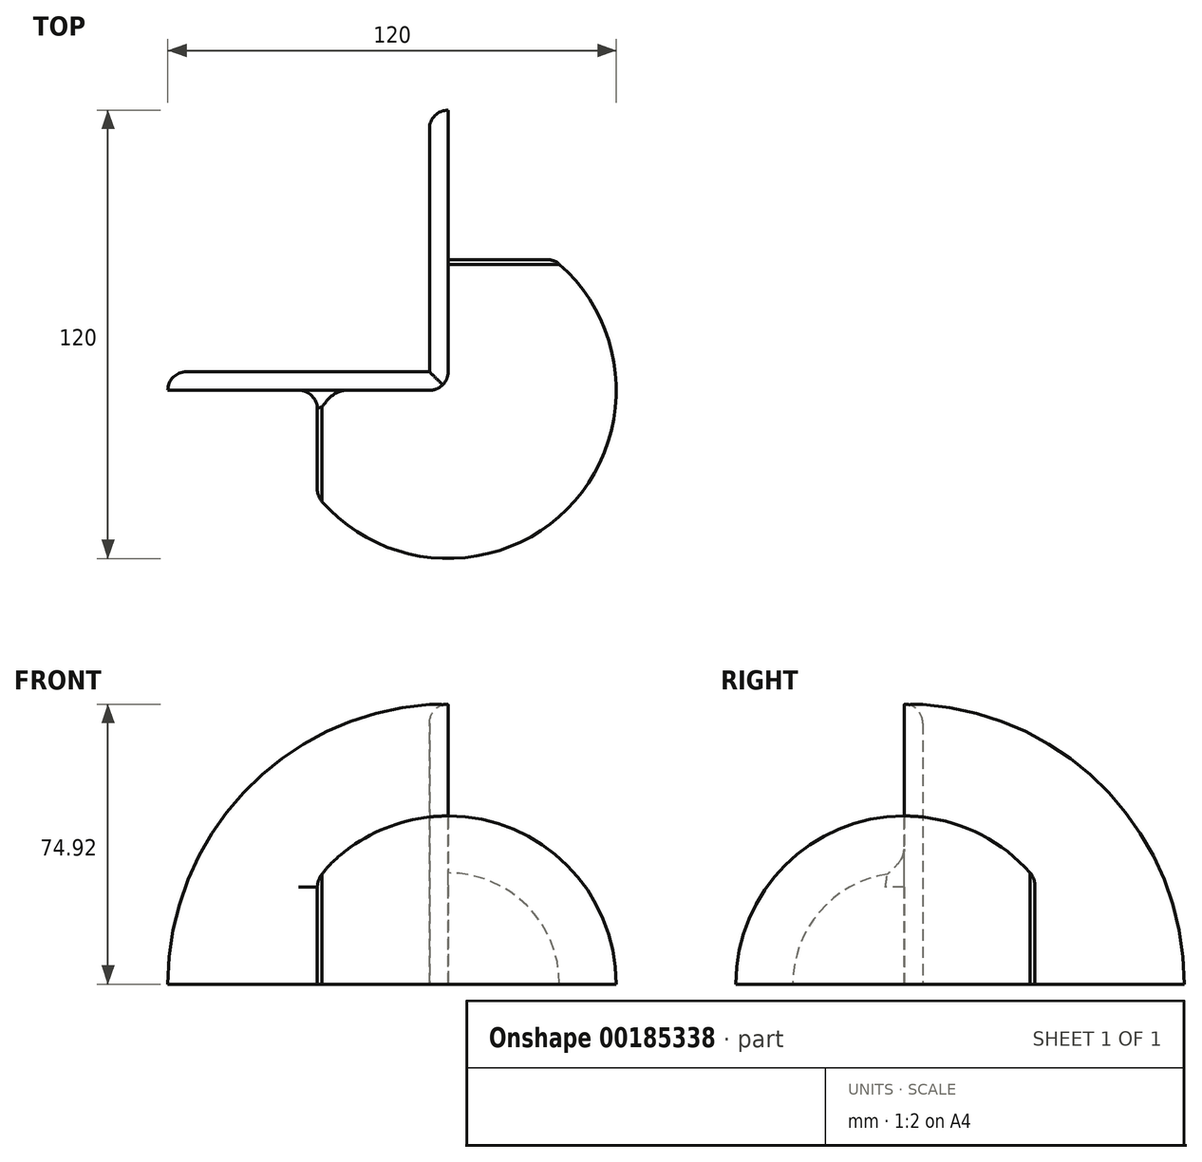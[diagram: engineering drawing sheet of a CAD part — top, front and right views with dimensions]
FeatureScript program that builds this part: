
annotation { "Feature Type Name" : "Feature", "Feature Type Description" : "" }
export const myFeature = defineFeature(function(context is Context, id is Id, definition is map)
    precondition{}
    {
        {
            var Q0;
            Q0=qCreatedBy(makeId("Front.planeOp"),FACE);
            var sketch = newSketch(context, id + "F0", { "sketchPlane" : qUnion([Q0])});
            skArc(sketch, "E0", {"start": v(0, 45) * mm, "mid": v(-31.82, 31.82) * mm, "end": v(-45, 0) * mm});
            skLineSegment(sketch, "E1", {"start": v(-45, 0) * mm, "end": v(0, 0) * mm});
            skLineSegment(sketch, "E2", {"start": v(0, 0) * mm, "end": v(0, 45) * mm});
            skSolve(sketch);
        }
        {
            var Q0;
            Q0 = qSketchRegion(id + "F0", true);
            var Q1;
            Q1=sQuery(id+"F0.wireOp",EDGE,"E2");
            revolve(context, id + "F1", {"entities" : qUnion([Q0]), "axis" : qUnion([Q1]), "revolveType" : RevolveType.ONE_DIRECTION, "angle" : 270 * degree});
        }
        {
            var Q0;
            Q0=makeQuery(id+"F1.opRevolve","CAP_FACE",FACE,{"disambiguationData":[OSD([sQuery(id+"F0.wireOp",EDGE,"E0"),sQuery(id+"F0.wireOp",EDGE,"E1"),sQuery(id+"F0.wireOp",EDGE,"E2")])],"isStart":true});
            var sketch = newSketch(context, id + "F2", { "sketchPlane" : qUnion([Q0])});
            skLineSegment(sketch, "E3", {"start": v(0, 0) * mm, "end": v(0, 75) * mm});
            skLineSegment(sketch, "E4", {"start": v(0, 0) * mm, "end": v(75, 0) * mm});
            skArc(sketch, "E5", {"start": v(75, 0) * mm, "mid": v(53.03, 53.03) * mm, "end": v(0, 75) * mm});
            skSolve(sketch);
        }
        {
            var Q0;
            Q0 = qSketchRegion(id + "F2", true);
            var Q1;
            Q1=sQuery(id+"F2.wireOp",EDGE,"E3");
            revolve(context, id + "F3", {"operationType" : NewBodyOperationType.ADD, "entities" : qUnion([Q0]), "axis" : qUnion([Q1]), "revolveType" : RevolveType.ONE_DIRECTION, "oppositeDirection" : true, "angle" : 90 * degree});
        }
        {
            var Q0;
            Q0=makeQuery(id+"F3.boolean.opBoolean","MERGE",FACE,{"derivedFrom":[makeQuery(id+"F1.opRevolve","SWEPT_FACE",FACE,{"disambiguationData":[OSD([sQuery(id+"F0.wireOp",EDGE,"E1")])]}),makeQuery(id+"F3.opRevolve","SWEPT_FACE",FACE,{"disambiguationData":[OSD([sQuery(id+"F2.wireOp",EDGE,"E4")])]})]});
            var sketch = newSketch(context, id + "F4", { "sketchPlane" : qUnion([Q0])});
            skLineSegment(sketch, "E6", {"start": v(-5, -74.83) * mm, "end": v(-5, -5) * mm});
            skLineSegment(sketch, "E7", {"start": v(-5, -5) * mm, "end": v(-74.83, -5) * mm});
            skArc(sketch, "E8.0", {"start": v(0, -75) * mm, "mid": v(-53.03, -53.03) * mm, "end": v(-75, 0) * mm});
            skLineSegment(sketch, "E9", {"start": v(-45, 0) * mm, "end": v(-35, 0) * mm});
            skLineSegment(sketch, "E10", {"start": v(-35, 0) * mm, "end": v(-35, 28.28) * mm});
            skArc(sketch, "E11.0", {"start": v(0, -45) * mm, "mid": v(31.82, 31.82) * mm, "end": v(-45, 0) * mm});
            skLineSegment(sketch, "E12", {"start": v(0, -35) * mm, "end": v(28.28, -35) * mm});
            skLineSegment(sketch, "E13", {"start": v(0, -35) * mm, "end": v(0, -45) * mm});
            skLineSegment(sketch, "E14", {"start": v(-5, -74.83) * mm, "end": v(10.24, -87.79) * mm});
            skLineSegment(sketch, "E15", {"start": v(10.24, -87.79) * mm, "end": v(15.24, -87.79) * mm});
            skLineSegment(sketch, "E16", {"start": v(15.24, -87.79) * mm, "end": v(0, -75) * mm});
            skPoint(sketch, "E17", {"position": v(-53.03, -53.03) * mm});
            skLineSegment(sketch, "E18", {"start": v(0, 0) * mm, "end": v(-53.03, -53.03) * mm, "construction": true});
            skLineSegment(sketch, "E19", {"start": v(-74.83, -5) * mm, "end": v(-88.25, 9.83) * mm});
            skLineSegment(sketch, "E20", {"start": v(-83.25, 9.83) * mm, "end": v(-75, 0) * mm});
            skLineSegment(sketch, "E21", {"start": v(-88.25, 9.83) * mm, "end": v(-83.25, 9.83) * mm});
            skSolve(sketch);
        }
        {
            var Q0;
            {var subQ0=sQuery(id+"F4.wireOp",EDGE,"E6");Q0=makeQuery(id+"F4.imprint","IMPRINT",FACE,{"disambiguationData":[TD([[makeQuery(id+"F4.imprint","IMPRINT",EDGE,{"derivedFrom":subQ0}),1.0]])]});}
            var Q1;
            {var subQ2=sQuery(id+"F4.wireOp",EDGE,"E12");Q1=makeQuery(id+"F4.imprint","IMPRINT",FACE,{"disambiguationData":[TD([[makeQuery(id+"F4.imprint","IMPRINT",EDGE,{"derivedFrom":subQ2}),-1.0]])]});}
            var Q2;
            {var subQ0=sQuery(id+"F4.wireOp",EDGE,"E9");Q2=makeQuery(id+"F4.imprint","IMPRINT",FACE,{"disambiguationData":[TD([[makeQuery(id+"F4.imprint","IMPRINT",EDGE,{"derivedFrom":subQ0}),1.0]])]});}
            extrude(context, id + "F5", {"entities" : qUnion([Q0, Q1, Q2]), "operationType" : NewBodyOperationType.REMOVE, "endBound" : BoundingType.THROUGH_ALL, "oppositeDirection" : true, "depth" : 25 * mm});
        }
        {
            var Q0;
            Q0=makeQuery(id+"F5.boolean.opBoolean","INTERSECT",EDGE,{"derivedFrom":[makeQuery(id+"F1.opRevolve","SWEPT_FACE",FACE,{"disambiguationData":[OSD([sQuery(id+"F0.wireOp",EDGE,"E0")])]}),makeQuery(id+"F5.opExtrude","SWEPT_FACE",FACE,{"disambiguationData":[OSD([sQuery(id+"F4.wireOp",EDGE,"E10")])]})]});
            var Q1;
            Q1=makeQuery(id+"F3.opRevolve","CAP_EDGE",EDGE,{"disambiguationData":[OSD([sQuery(id+"F2.wireOp",EDGE,"E5")])],"isStart":true});
            var Q2;
            Q2=makeQuery(id+"F5.boolean.opBoolean","INTERSECT",EDGE,{"derivedFrom":[makeQuery(id+"F3.opRevolve","SWEPT_FACE",FACE,{"disambiguationData":[OSD([sQuery(id+"F2.wireOp",EDGE,"E5")])]}),makeQuery(id+"F5.opExtrude","SWEPT_FACE",FACE,{"disambiguationData":[OSD([sQuery(id+"F4.wireOp",EDGE,"E7")])]})]});
            var Q3;
            Q3=makeQuery(id+"F5.boolean.opBoolean","INTERSECT",EDGE,{"derivedFrom":[makeQuery(id+"F3.opRevolve","SWEPT_FACE",FACE,{"disambiguationData":[OSD([sQuery(id+"F2.wireOp",EDGE,"E5")])]}),makeQuery(id+"F5.opExtrude","SWEPT_FACE",FACE,{"disambiguationData":[OSD([sQuery(id+"F4.wireOp",EDGE,"E6")])]})]});
            var Q4;
            Q4=makeQuery(id+"F3.opRevolve","CAP_EDGE",EDGE,{"disambiguationData":[OSD([sQuery(id+"F2.wireOp",EDGE,"E5")])],"isStart":false});
            var Q5;
            Q5=makeQuery(id+"F5.boolean.opBoolean","INTERSECT",EDGE,{"derivedFrom":[makeQuery(id+"F1.opRevolve","SWEPT_FACE",FACE,{"disambiguationData":[OSD([sQuery(id+"F0.wireOp",EDGE,"E0")])]}),makeQuery(id+"F5.opExtrude","SWEPT_FACE",FACE,{"disambiguationData":[OSD([sQuery(id+"F4.wireOp",EDGE,"E12")])]})]});
            var Q6;
            Q6=makeQuery(id+"F5.boolean.opBoolean","COPY",EDGE,{"derivedFrom":makeQuery(id+"F5.opExtrude","SWEPT_EDGE",EDGE,{"disambiguationData":[OSD([sQuery(id+"F4.wireOp",EDGE,"E9"),sQuery(id+"F4.wireOp",EDGE,"E10")])]})});
            var Q7;
            Q7=makeQuery(id+"F1.opRevolve","CAP_EDGE",EDGE,{"disambiguationData":[OSD([sQuery(id+"F0.wireOp",EDGE,"E0")])],"isStart":false});
            fillet(context, id + "F6", {"entities" : qUnion([Q0, Q1, Q2, Q3, Q4, Q5, Q6, Q7]), "radius" : 5 * mm, "tangentPropagation" : true, "allowEdgeOverflow" : false});
        }
        {
            var Q0;
            Q0=makeQuery(id+"F3.opRevolve","CAP_EDGE",EDGE,{"disambiguationData":[OSD([sQuery(id+"F2.wireOp",EDGE,"E3")])],"isStart":true});
            fillet(context, id + "F7", {"entities" : qUnion([Q0]), "radius" : 5 * mm, "tangentPropagation" : true, "allowEdgeOverflow" : false});
        }
    });
